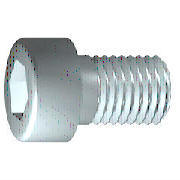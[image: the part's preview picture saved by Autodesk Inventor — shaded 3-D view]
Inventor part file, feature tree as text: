
AUTODESK INVENTOR PART (.ipt)
format: ipt  version: 2019 (Build 230136000, 136)  size: 190,976 bytes
history: native  units: mm (DEFAULTED — no unit token found)
features: sketch x2, extrude x1, plane x1, fillet x1
ambient origin geometry x7: Origin, YZ Plane, XY Plane, X Axis, Y Axis, Z Axis, Center Point
bodies: Solid1 (feature_tree), Body (feature_tree)
feature tree (5):
  extrude  "Slot"  Depth=3.5052mm
  plane  "Work Plane1"
  fillet  "Fillet2"  Radius=3.5052mm
  sketch  "Sketch1"  dims[d1=10.715552mm d2=1.984348mm d3=3.5052mm]
  sketch  "Sketch2"  dims[d4=1.6256mm d5=60.0deg d6=3.5052mm d7=3.5052mm d8=3.196904mm d9=5.7404mm d10=90.0deg d11=10.0mm d12=0.0mm d13=10.715552mm d14=0.0mm d15=0.47244mm d16=0.47244mm d17=0.3302mm d19=0.0mm d26=12.7mm d27=45.0deg d28=0.0mm d29=0.0mm d30=0.127mm]
